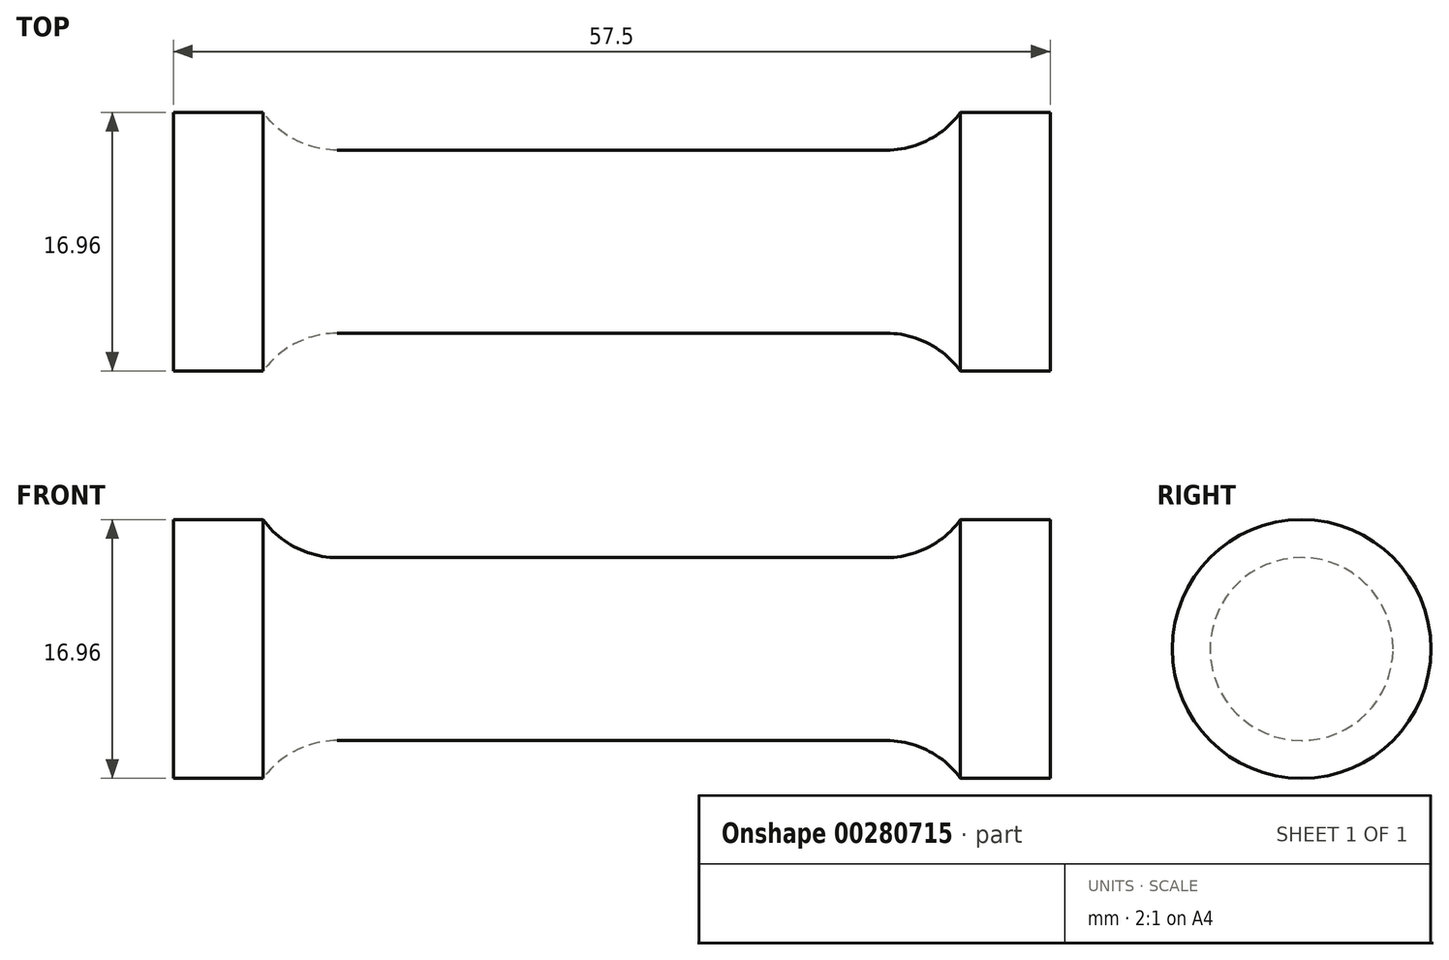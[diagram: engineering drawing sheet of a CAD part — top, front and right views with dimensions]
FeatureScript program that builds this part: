
annotation { "Feature Type Name" : "Feature", "Feature Type Description" : "" }
export const myFeature = defineFeature(function(context is Context, id is Id, definition is map)
    precondition{}
    {
        {
            var Q0;
            Q0=qCreatedBy(makeId("Front.planeOp"),FACE);
            var sketch = newSketch(context, id + "F0", { "sketchPlane" : qUnion([Q0])});
            skLineSegment(sketch, "E0", {"start": v(0, 6) * mm, "end": v(18, 6) * mm});
            skArc(sketch, "E1", {"start": v(18, 6) * mm, "mid": v(20.73, 6.66) * mm, "end": v(22.86, 8.48) * mm});
            skLineSegment(sketch, "E2", {"start": v(22.86, 8.48) * mm, "end": v(28.75, 8.48) * mm});
            skLineSegment(sketch, "E3", {"start": v(28.75, 8.48) * mm, "end": v(28.75, 0) * mm});
            skLineSegment(sketch, "E4.MirrorCS", {"start": v(0, 6) * mm, "end": v(-18, 6) * mm});
            skLineSegment(sketch, "E5.MirrorCS", {"start": v(-28.75, 8.48) * mm, "end": v(-28.75, 0) * mm});
            skLineSegment(sketch, "E6.MirrorCS", {"start": v(-22.86, 8.48) * mm, "end": v(-28.75, 8.48) * mm});
            skArc(sketch, "E7.MirrorCS", {"start": v(-18, 6) * mm, "mid": v(-20.73, 6.66) * mm, "end": v(-22.86, 8.48) * mm});
            skLineSegment(sketch, "E8", {"start": v(-28.75, 0) * mm, "end": v(28.75, 0) * mm});
            skSolve(sketch);
        }
        {
            var Q0;
            Q0 = qSketchRegion(id + "F0", true);
            var Q1;
            Q1=sQuery(id+"F0.wireOp",EDGE,"E8");
            revolve(context, id + "F1", {"entities" : qUnion([Q0]), "axis" : qUnion([Q1]), "revolveType" : RevolveType.FULL});
        }
    });
